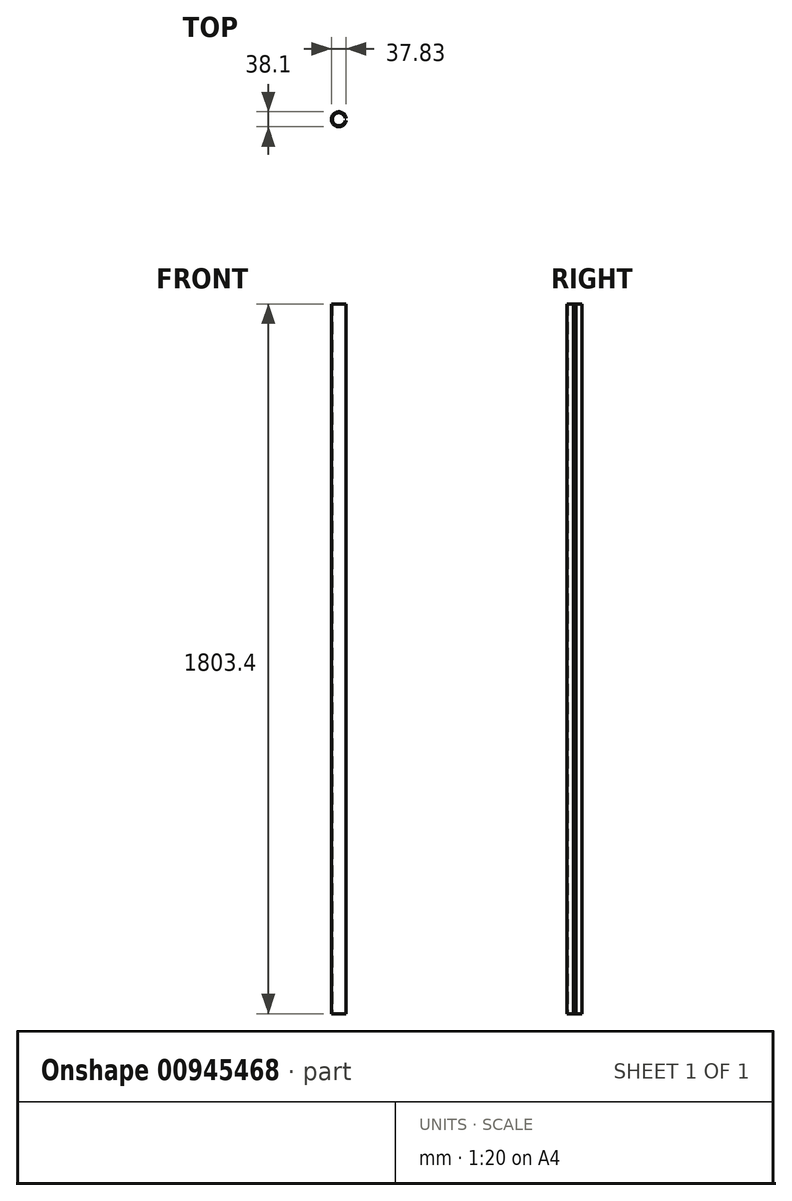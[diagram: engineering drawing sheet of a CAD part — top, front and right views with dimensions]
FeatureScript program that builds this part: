
annotation { "Feature Type Name" : "Feature", "Feature Type Description" : "" }
export const myFeature = defineFeature(function(context is Context, id is Id, definition is map)
    precondition{}
    {
        {
            var Q0;
            Q0=qCreatedBy(makeId("Top.planeOp"),FACE);
            var sketch = newSketch(context, id + "F0", { "sketchPlane" : qUnion([Q0])});
            skCircle(sketch, "E0", {"center": v(-46.6, 0) * mm, "radius": 19.05 * mm});
            skSolve(sketch);
        }
        {
            var Q0;
            Q0 = qSketchRegion(id + "F0", true);
            extrude(context, id + "F1", {"entities" : qUnion([Q0]), "depth" : 1828.8 * mm, "offsetDistance" : 25.4 * mm});
        }
        {
            var Q0;
            Q0=makeQuery(id+"F1.opExtrude","CAP_FACE",FACE,{"disambiguationData":[OSD([sQuery(id+"F0.wireOp",EDGE,"E0")])],"isStart":true});
            shell(context, id + "F2", {"entities" : qUnion([Q0]), "thickness" : 2.54 * mm});
        }
        {
            var Q0;
            Q0=makeQuery(id+"F1.opExtrude","CAP_FACE",FACE,{"disambiguationData":[OSD([sQuery(id+"F0.wireOp",EDGE,"E0")])],"isStart":false});
            extrude(context, id + "F3", {"entities" : qUnion([Q0]), "operationType" : NewBodyOperationType.REMOVE, "oppositeDirection" : true, "depth" : 25.4 * mm, "offsetDistance" : 25.4 * mm});
        }
        {
            var Q0;
            Q0=qCreatedBy(makeId("Right.planeOp"),FACE);
            cPlane(context, id + "F4", {"entities" : qUnion([Q0]), "cplaneType" : CPlaneType.OFFSET, "offset" : 25.4 * mm, "oppositeDirection" : true, "width" : 152.4 * mm, "height" : 152.4 * mm});
        }
        {
            var Q0;
            Q0=qCreatedBy(id+"F4.planeOp",FACE);
            var sketch = newSketch(context, id + "F5", { "sketchPlane" : qUnion([Q0])});
            skLineSegment(sketch, "E1.bottom", {"start": v(3.17, 17438.53) * mm, "end": v(-3.18, 17438.53) * mm});
            skLineSegment(sketch, "E1.top", {"start": v(3.17, -13041.47) * mm, "end": v(-3.18, -13041.47) * mm});
            skLineSegment(sketch, "E1.left", {"start": v(3.17, 17438.53) * mm, "end": v(3.17, -13041.47) * mm});
            skLineSegment(sketch, "E1.right", {"start": v(-3.18, 17438.53) * mm, "end": v(-3.18, -13041.47) * mm});
            skPoint(sketch, "E1.middle", {"position": v(0, 2198.53) * mm});
            skSolve(sketch);
        }
        {
            var Q0;
            Q0 = qSketchRegion(id + "F5", true);
            extrude(context, id + "F6", {"entities" : qUnion([Q0]), "operationType" : NewBodyOperationType.REMOVE, "oppositeDirection" : true, "depth" : 25.4 * mm, "offsetDistance" : 25.4 * mm});
        }
    });
